# Revit family: TESK_Насос вертикальный_SVM(T)-1
name_source: partatom
category: Оборудование
units: mm (PartAtom-declared; Revit-internal decimal feet)

## family parameters
Всегда вертикально = Да
Классификация = Насос
На основе рабочей плоскости = Нет
Общий = Нет
При загрузке вырезать с полостями = Нет
Размер круглого соединителя = Использовать диаметр
Тип детали = Вставляется
Точка расчета площади = Нет

## types (44) — shared parameters
ADSK_Версия Revit = 2019
ADSK_Версия семейства = 1.0
ADSK_Диаметр условный = 25 мм
ADSK_Единица измерения = шт.
ADSK_Завод-изготовитель = TESK
ADSK_Классификация нагрузок = Прочее
ADSK_Количество = 1
ADSK_Количество фаз = 3
ADSK_Количество фаз числовое = 3
ADSK_Коэффициент мощности = 1
ADSK_Наименование краткое = Вертикальный многоступенчатый центробежный насос
ADSK_Напряжение = 400 В
URL = www.teskpump.ru
Длина_ВспомЛиния = 30 мм
Материал_1 = TESK_Черный_Условный
Материал_2 = TESK_Нержавеющая сталь
Материал_КорпусДвигателя = TESK_Черный_Ребра_Условный
Таблица_Поиска = TESK_SVM(T)-1
УГО_Длина = 250 мм
Фланец_Толщина = 18 мм

## per-type parameters (varying)
| type | ADSK_Код изделия | ADSK_Масса | ADSK_Масса_Текст | ADSK_Наименование | ADSK_Номинальная мощность | ADSK_Полная мощность | Высота_Корпуса | Высота_Перехода | Двигатель_Высота | Двигатель_ОтступКоробки | Двигатель_Ширина | Материал_КорпусУлитка | Напор максимальный |
| SVM 1-2 0.37kW 3x380V 50Hz IE3 | 771-20003380NSSF | 20 | 20 | Вертикальный многоступенчатый центробежный насос SVM, DN25, PN25, Hmax=13м (3x380V 50Hz IE3) | 0 кВт | 0 кВ·А | 258 мм | 90 мм | 239 мм | 117 мм | 148 мм | TESK_Нержавеющая сталь | 13 |
| SVM 1-3 0.37kW 3x380V 50Hz IE3 | 771-30003380NSSF | 20 | 20 | Вертикальный многоступенчатый центробежный насос SVM, DN25, PN25, Hmax=19м (3x380V 50Hz IE3) | 0 кВт | 0 кВ·А | 276 мм | 90 мм | 239 мм | 117 мм | 148 мм | TESK_Нержавеющая сталь | 19 |
| SVM 1-4 0.37kW 3x380V 50Hz IE3 | 771-40003380NSSF | 21 | 21 | Вертикальный многоступенчатый центробежный насос SVM, DN25, PN25, Hmax=24м (3x380V 50Hz IE3) | 0 кВт | 0 кВ·А | 294 мм | 90 мм | 239 мм | 117 мм | 148 мм | TESK_Нержавеющая сталь | 24 |
| SVM 1-5 0.37kW 3x380V 50Hz IE3 | 771-50003380NSSF | 21 | 21 | Вертикальный многоступенчатый центробежный насос SVM, DN25, PN25, Hmax=30м (3x380V 50Hz IE3) | 0 кВт | 0 кВ·А | 312 мм | 90 мм | 239 мм | 117 мм | 148 мм | TESK_Нержавеющая сталь | 30 |
| SVM 1-6 0.37kW 3x380V 50Hz IE3 | 771-60003380NSSF | 22 | 22 | Вертикальный многоступенчатый центробежный насос SVM, DN25, PN25, Hmax=36м (3x380V 50Hz IE3) | 0 кВт | 0 кВ·А | 330 мм | 90 мм | 239 мм | 117 мм | 148 мм | TESK_Нержавеющая сталь | 36 |
| SVM 1-7 0.37kW 3x380V 50Hz IE3 | 771-70003380NSSF | 23 | 23 | Вертикальный многоступенчатый центробежный насос SVM, DN25, PN25, Hmax=42м (3x380V 50Hz IE3) | 0 кВт | 0 кВ·А | 348 мм | 90 мм | 239 мм | 117 мм | 148 мм | TESK_Нержавеющая сталь | 42 |
| SVM 1-8 0.55kW 3x380V 50Hz IE3 | 771-80003380NSSF | 24 | 24 | Вертикальный многоступенчатый центробежный насос SVM, DN25, PN25, Hmax=48м (3x380V 50Hz IE3) | 1 кВт | 1 кВ·А | 366 мм | 90 мм | 239 мм | 117 мм | 148 мм | TESK_Нержавеющая сталь | 48 |
| SVM 1-9 0.55kW 3x380V 50Hz IE3 | 771-90003380NSSF | 25 | 25 | Вертикальный многоступенчатый центробежный насос SVM, DN25, PN25, Hmax=54м (3x380V 50Hz IE3) | 1 кВт | 1 кВ·А | 384 мм | 90 мм | 239 мм | 117 мм | 148 мм | TESK_Нержавеющая сталь | 54 |
| SVM 1-10 0.55kW 3x380V 50Hz IE3 | 771-100003380NSSF | 26 | 26 | Вертикальный многоступенчатый центробежный насос SVM, DN25, PN25, Hmax=60м (3x380V 50Hz IE3) | 1 кВт | 1 кВ·А | 402 мм | 90 мм | 239 мм | 117 мм | 148 мм | TESK_Нержавеющая сталь | 60 |
| SVM 1-11 0.55kW 3x380V 50Hz IE3 | 771-110003380NSSF | 26 | 26 | Вертикальный многоступенчатый центробежный насос SVM, DN25, PN25, Hmax=66м (3x380V 50Hz IE3) | 1 кВт | 1 кВ·А | 420 мм | 90 мм | 239 мм | 117 мм | 148 мм | TESK_Нержавеющая сталь | 66 |
| SVM 1-12 0.75kW 3x380V 50Hz IE3 | 771-120003380NSSF | 29 | 29 | Вертикальный многоступенчатый центробежный насос SVM, DN25, PN25, Hmax=72м (3x380V 50Hz IE3) | 1 кВт | 1 кВ·А | 448 мм | 110 мм | 280 мм | 142 мм | 170 мм | TESK_Нержавеющая сталь | 72 |
| SVM 1-13 0.75kW 3x380V 50Hz IE3 | 771-130003380NSSF | 30 | 30 | Вертикальный многоступенчатый центробежный насос SVM, DN25, PN25, Hmax=78м (3x380V 50Hz IE3) | 1 кВт | 1 кВ·А | 466 мм | 110 мм | 280 мм | 142 мм | 170 мм | TESK_Нержавеющая сталь | 78 |
| SVM 1-15 0.75kW 3x380V 50Hz IE3 | 771-150003380NSSF | 31 | 31 | Вертикальный многоступенчатый центробежный насос SVM, DN25, PN25, Hmax=89м (3x380V 50Hz IE3) | 1 кВт | 1 кВ·А | 502 мм | 110 мм | 280 мм | 142 мм | 170 мм | TESK_Нержавеющая сталь | 89 |
| SVM 1-17 1.1kW 3x380V 50Hz IE3 | 771-170003380NSSF | 33 | 33 | Вертикальный многоступенчатый центробежный насос SVM, DN25, PN25, Hmax=101м (3x380V 50Hz IE3) | 1 кВт | 1 кВ·А | 538 мм | 110 мм | 280 мм | 142 мм | 170 мм | TESK_Нержавеющая сталь | 101 |
| SVM 1-19 1.1kW 3x380V 50Hz IE3 | 771-190003380NSSF | 34 | 34 | Вертикальный многоступенчатый центробежный насос SVM, DN25, PN25, Hmax=113м (3x380V 50Hz IE3) | 1 кВт | 1 кВ·А | 574 мм | 110 мм | 280 мм | 142 мм | 170 мм | TESK_Нержавеющая сталь | 113 |
| SVM 1-21 1.1kW 3x380V 50Hz IE3 | 771-210003380NSSF | 35 | 35 | Вертикальный многоступенчатый центробежный насос SVM, DN25, PN25, Hmax=124м (3x380V 50Hz IE3) | 1 кВт | 1 кВ·А | 610 мм | 110 мм | 280 мм | 142 мм | 170 мм | TESK_Нержавеющая сталь | 124 |
| SVM 1-23 1.1kW 3x380V 50Hz IE3 | 771-230003380NSSF | 36 | 36 | Вертикальный многоступенчатый центробежный насос SVM, DN25, PN25, Hmax=137м (3x380V 50Hz IE3) | 1 кВт | 1 кВ·А | 646 мм | 110 мм | 280 мм | 142 мм | 170 мм | TESK_Нержавеющая сталь | 137 |
| SVM 1-25 1.5kW 3x380V 50Hz IE3 | 771-250003380NSSF | 42 | 42 | Вертикальный многоступенчатый центробежный насос SVM, DN25, PN25, Hmax=149м (3x380V 50Hz IE3) | 2 кВт | 2 кВ·А | 692 мм | 130 мм | 333 мм | 155 мм | 190 мм | TESK_Нержавеющая сталь | 149 |
| SVM 1-27 1.5kW 3x380V 50Hz IE3 | 771-270003380NSSF | 43 | 43 | Вертикальный многоступенчатый центробежный насос SVM, DN25, PN25, Hmax=161м (3x380V 50Hz IE3) | 2 кВт | 2 кВ·А | 728 мм | 130 мм | 333 мм | 155 мм | 190 мм | TESK_Нержавеющая сталь | 161 |
| SVM 1-30 1.5kW 3x380V 50Hz IE3 | 771-300003380NSSF | 45 | 45 | Вертикальный многоступенчатый центробежный насос SVM, DN25, PN25, Hmax=178м (3x380V 50Hz IE3) | 2 кВт | 2 кВ·А | 782 мм | 130 мм | 333 мм | 155 мм | 190 мм | TESK_Нержавеющая сталь | 178 |
| SVM 1-33 2.2kW 3x380V 50Hz IE3 | 771-330003380NSSF | 49 | 49 | Вертикальный многоступенчатый центробежный насос SVM, DN25, PN25, Hmax=196м (3x380V 50Hz IE3) | 2 кВт | 2 кВ·А | 836 мм | 130 мм | 333 мм | 155 мм | 190 мм | TESK_Нержавеющая сталь | 196 |
| SVM 1-36 2.2kW 3x380V 50Hz IE3 | 771-360003380NSSF | 51 | 51 | Вертикальный многоступенчатый центробежный насос SVM, DN25, PN25, Hmax=214м (3x380V 50Hz IE3) | 2 кВт | 2 кВ·А | 890 мм | 130 мм | 333 мм | 155 мм | 190 мм | TESK_Нержавеющая сталь | 214 |
| SVMT 1-2 0.37kW 3x380V 50Hz IE3 | 771-20003380N | 20 | 20 | Вертикальный многоступенчатый центробежный насос SVMT, DN25, PN25, Hmax=13м (3x380V 50Hz IE3) | 0 кВт | 0 кВ·А | 258 мм | 90 мм | 239 мм | 117 мм | 148 мм | TESK_Черный_Условный | 13 |
| SVMT 1-3 0.37kW 3x380V 50Hz IE3 | 771-30003380N | 20 | 20 | Вертикальный многоступенчатый центробежный насос SVMT, DN25, PN25, Hmax=19м (3x380V 50Hz IE3) | 0 кВт | 0 кВ·А | 276 мм | 90 мм | 239 мм | 117 мм | 148 мм | TESK_Черный_Условный | 19 |
| SVMT 1-4 0.37kW 3x380V 50Hz IE3 | 771-40003380N | 21 | 21 | Вертикальный многоступенчатый центробежный насос SVMT, DN25, PN25, Hmax=24м (3x380V 50Hz IE3) | 0 кВт | 0 кВ·А | 294 мм | 90 мм | 239 мм | 117 мм | 148 мм | TESK_Черный_Условный | 24 |
| SVMT 1-5 0.37kW 3x380V 50Hz IE3 | 771-50003380N | 21 | 21 | Вертикальный многоступенчатый центробежный насос SVMT, DN25, PN25, Hmax=30м (3x380V 50Hz IE3) | 0 кВт | 0 кВ·А | 312 мм | 90 мм | 239 мм | 117 мм | 148 мм | TESK_Черный_Условный | 30 |
| SVMT 1-6 0.37kW 3x380V 50Hz IE3 | 771-60003380N | 22 | 22 | Вертикальный многоступенчатый центробежный насос SVMT, DN25, PN25, Hmax=36м (3x380V 50Hz IE3) | 0 кВт | 0 кВ·А | 330 мм | 90 мм | 239 мм | 117 мм | 148 мм | TESK_Черный_Условный | 36 |
| SVMT 1-7 0.37kW 3x380V 50Hz IE3 | 771-70003380N | 23 | 23 | Вертикальный многоступенчатый центробежный насос SVMT, DN25, PN25, Hmax=42м (3x380V 50Hz IE3) | 0 кВт | 0 кВ·А | 348 мм | 90 мм | 239 мм | 117 мм | 148 мм | TESK_Черный_Условный | 42 |
| SVMT 1-8 0.55kW 3x380V 50Hz IE3 | 771-80003380N | 24 | 24 | Вертикальный многоступенчатый центробежный насос SVMT, DN25, PN25, Hmax=48м (3x380V 50Hz IE3) | 1 кВт | 1 кВ·А | 366 мм | 90 мм | 239 мм | 117 мм | 148 мм | TESK_Черный_Условный | 48 |
| SVMT 1-9 0.55kW 3x380V 50Hz IE3 | 771-90003380N | 25 | 25 | Вертикальный многоступенчатый центробежный насос SVMT, DN25, PN25, Hmax=54м (3x380V 50Hz IE3) | 1 кВт | 1 кВ·А | 384 мм | 90 мм | 239 мм | 117 мм | 148 мм | TESK_Черный_Условный | 54 |
| SVMT 1-10 0.55kW 3x380V 50Hz IE3 | 771-100003380N | 26 | 26 | Вертикальный многоступенчатый центробежный насос SVMT, DN25, PN25, Hmax=60м (3x380V 50Hz IE3) | 1 кВт | 1 кВ·А | 402 мм | 90 мм | 239 мм | 117 мм | 148 мм | TESK_Черный_Условный | 60 |
| SVMT 1-11 0.55kW 3x380V 50Hz IE3 | 771-110003380N | 26 | 26 | Вертикальный многоступенчатый центробежный насос SVMT, DN25, PN25, Hmax=66м (3x380V 50Hz IE3) | 1 кВт | 1 кВ·А | 420 мм | 90 мм | 239 мм | 117 мм | 148 мм | TESK_Черный_Условный | 66 |
| SVMT 1-12 0.75kW 3x380V 50Hz IE3 | 771-120003380N | 29 | 29 | Вертикальный многоступенчатый центробежный насос SVMT, DN25, PN25, Hmax=72м (3x380V 50Hz IE3) | 1 кВт | 1 кВ·А | 448 мм | 110 мм | 280 мм | 142 мм | 170 мм | TESK_Черный_Условный | 72 |
| SVMT 1-13 0.75kW 3x380V 50Hz IE3 | 771-130003380N | 30 | 30 | Вертикальный многоступенчатый центробежный насос SVMT, DN25, PN25, Hmax=78м (3x380V 50Hz IE3) | 1 кВт | 1 кВ·А | 466 мм | 110 мм | 280 мм | 142 мм | 170 мм | TESK_Черный_Условный | 78 |
| SVMT 1-15 0.75kW 3x380V 50Hz IE3 | 771-150003380N | 31 | 31 | Вертикальный многоступенчатый центробежный насос SVMT, DN25, PN25, Hmax=89м (3x380V 50Hz IE3) | 1 кВт | 1 кВ·А | 502 мм | 110 мм | 280 мм | 142 мм | 170 мм | TESK_Черный_Условный | 89 |
| SVMT 1-17 1.1kW 3x380V 50Hz IE3 | 771-170003380N | 33 | 33 | Вертикальный многоступенчатый центробежный насос SVMT, DN25, PN25, Hmax=101м (3x380V 50Hz IE3) | 1 кВт | 1 кВ·А | 538 мм | 110 мм | 280 мм | 142 мм | 170 мм | TESK_Черный_Условный | 101 |
| SVMT 1-19 1.1kW 3x380V 50Hz IE3 | 771-190003380N | 34 | 34 | Вертикальный многоступенчатый центробежный насос SVMT, DN25, PN25, Hmax=113м (3x380V 50Hz IE3) | 1 кВт | 1 кВ·А | 574 мм | 110 мм | 280 мм | 142 мм | 170 мм | TESK_Черный_Условный | 113 |
| SVMT 1-21 1.1kW 3x380V 50Hz IE3 | 771-210003380N | 35 | 35 | Вертикальный многоступенчатый центробежный насос SVMT, DN25, PN25, Hmax=124м (3x380V 50Hz IE3) | 1 кВт | 1 кВ·А | 610 мм | 110 мм | 280 мм | 142 мм | 170 мм | TESK_Черный_Условный | 124 |
| SVMT 1-23 1.1kW 3x380V 50Hz IE3 | 771-230003380N | 36 | 36 | Вертикальный многоступенчатый центробежный насос SVMT, DN25, PN25, Hmax=137м (3x380V 50Hz IE3) | 1 кВт | 1 кВ·А | 646 мм | 110 мм | 280 мм | 142 мм | 170 мм | TESK_Черный_Условный | 137 |
| SVMT 1-25 1.5kW 3x380V 50Hz IE3 | 771-250003380N | 42 | 42 | Вертикальный многоступенчатый центробежный насос SVMT, DN25, PN25, Hmax=149м (3x380V 50Hz IE3) | 2 кВт | 2 кВ·А | 692 мм | 130 мм | 333 мм | 155 мм | 190 мм | TESK_Черный_Условный | 149 |
| SVMT 1-27 1.5kW 3x380V 50Hz IE3 | 771-270003380N | 43 | 43 | Вертикальный многоступенчатый центробежный насос SVMT, DN25, PN25, Hmax=161м (3x380V 50Hz IE3) | 2 кВт | 2 кВ·А | 728 мм | 130 мм | 333 мм | 155 мм | 190 мм | TESK_Черный_Условный | 161 |
| SVMT 1-30 1.5kW 3x380V 50Hz IE3 | 771-300003380N | 45 | 45 | Вертикальный многоступенчатый центробежный насос SVMT, DN25, PN25, Hmax=178м (3x380V 50Hz IE3) | 2 кВт | 2 кВ·А | 782 мм | 130 мм | 333 мм | 155 мм | 190 мм | TESK_Черный_Условный | 178 |
| SVMT 1-33 2.2kW 3x380V 50Hz IE3 | 771-330003380N | 49 | 49 | Вертикальный многоступенчатый центробежный насос SVMT, DN25, PN25, Hmax=196м (3x380V 50Hz IE3) | 2 кВт | 2 кВ·А | 836 мм | 130 мм | 333 мм | 155 мм | 190 мм | TESK_Черный_Условный | 196 |
| SVMT 1-36 2.2kW 3x380V 50Hz IE3 | 771-360003380N | 51 | 51 | Вертикальный многоступенчатый центробежный насос SVMT, DN25, PN25, Hmax=214м (3x380V 50Hz IE3) | 2 кВт | 2 кВ·А | 890 мм | 130 мм | 333 мм | 155 мм | 190 мм | TESK_Черный_Условный | 214 |

note: column(s) folded — value = type name in every type: ADSK_Марка
